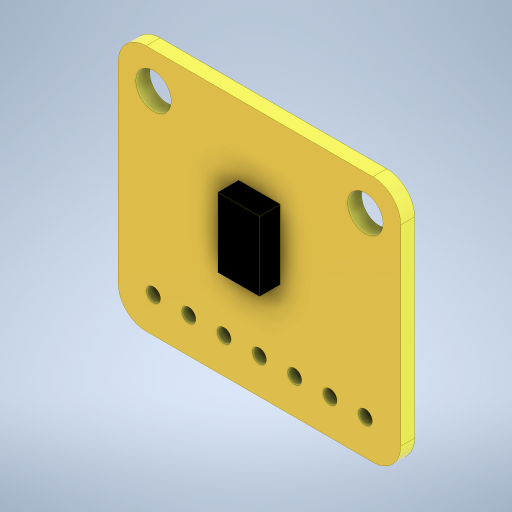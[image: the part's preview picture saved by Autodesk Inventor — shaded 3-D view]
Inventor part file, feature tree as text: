
AUTODESK INVENTOR PART (.ipt)
format: ipt  version: 2023 (Build 270158000, 158)  size: 275,968 bytes
history: native  units: mm
features: extrude x2, sketch x2
ambient origin geometry x8: Origin, YZ Plane, XZ Plane, XY Plane, X Axis, Y Axis, Z Axis, Center Point
bodies: Solid1 (feature_tree)
feature tree (4):
  extrude  "Extrusion1"  Depth=17.78mm
  extrude  "Extrusion2"  Depth=1.5mm
  sketch  "Sketch1"  dims[d0=20.32mm d1=17.78mm]
  sketch  "Sketch2"  dims[d2=15.24mm d3=2.54mm d4=2.54mm d5=2.0mm d6=1.0mm d7=0.0mm d8=2.54mm d9=1.0mm d10=40.0mm d12=2.54mm d13=40.0mm d15=2.54mm d18=3.0mm d19=5.0mm d21=7.5mm d22=1.5mm d23=0.0mm]
